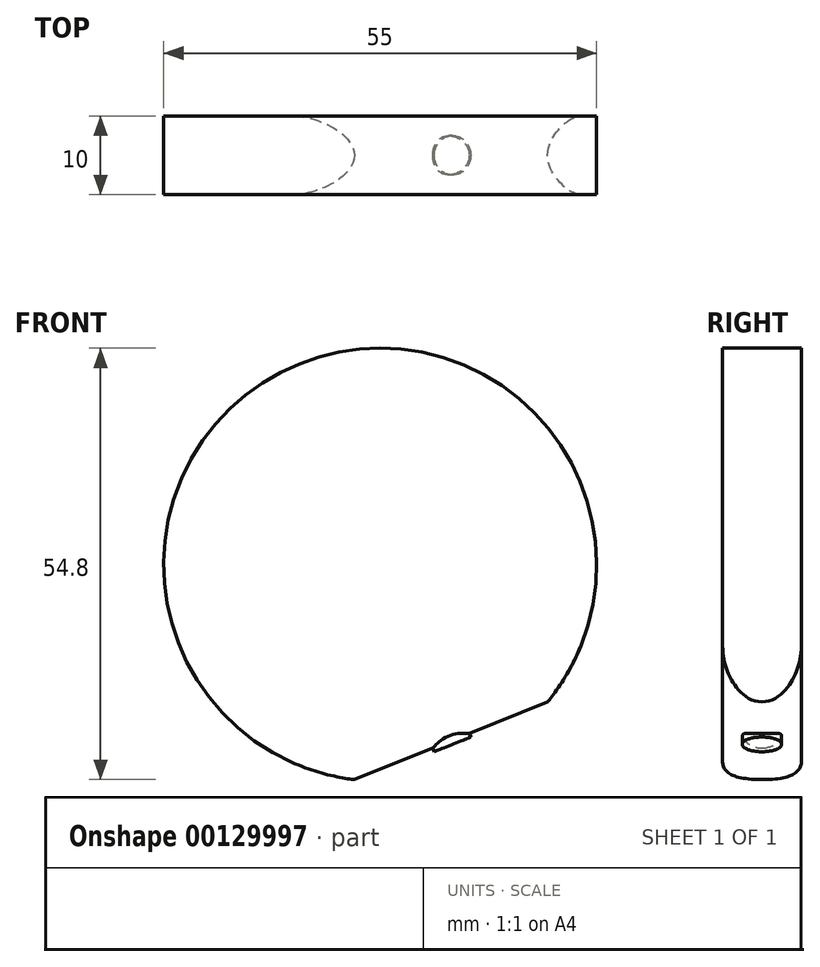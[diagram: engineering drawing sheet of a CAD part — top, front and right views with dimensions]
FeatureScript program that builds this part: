
annotation { "Feature Type Name" : "Feature", "Feature Type Description" : "" }
export const myFeature = defineFeature(function(context is Context, id is Id, definition is map)
    precondition{}
    {
        {
            var Q0;
            Q0=qCreatedBy(makeId("Front.planeOp"),FACE);
            var sketch = newSketch(context, id + "F0", { "sketchPlane" : qUnion([Q0])});
            skArc(sketch, "E0", {"start": v(5.8, 11.17) * mm, "mid": v(-25.73, 54.11) * mm, "end": v(-18.72, 1.3) * mm});
            skLineSegment(sketch, "E1", {"start": v(5.8, 11.17) * mm, "end": v(-18.72, 1.3) * mm});
            skSolve(sketch);
        }
        {
            var Q0;
            Q0=makeQuery(id+"F0.imprint","IMPRINT",FACE,{"disambiguationData":[TD([[makeQuery(id+"F0.imprint","IMPRINT",EDGE,{"derivedFrom":sQuery(id+"F0.wireOp",EDGE,"E0")}),1.0]])]});
            extrude(context, id + "F1", {"entities" : qUnion([Q0]), "depth" : 10 * mm});
        }
        {
            var Q0;
            Q0=makeQuery(id+"F1.opExtrude","SWEPT_FACE",FACE,{"disambiguationData":[OSD([sQuery(id+"F0.wireOp",EDGE,"E1")])]});
            var sketch = newSketch(context, id + "F2", { "sketchPlane" : qUnion([Q0])});
            skCircle(sketch, "E2", {"center": v(-3.67, 5) * mm, "radius": 2.5 * mm});
            skPoint(sketch, "E2.centerSnap0", {"position": v(-3.67, 10) * mm});
            skSolve(sketch);
        }
        {
            var Q0;
            Q0 = qSketchRegion(id + "F2", true);
            extrude(context, id + "F3", {"entities" : qUnion([Q0]), "operationType" : NewBodyOperationType.ADD, "depth" : 0.5 * mm});
        }
        {
            var Q0;
            Q0=makeQuery(id+"F1.opExtrude","CAP_EDGE",EDGE,{"disambiguationData":[OSD([sQuery(id+"F0.wireOp",EDGE,"E1")])],"isStart":false});
            var Q1;
            Q1=makeQuery(id+"F1.opExtrude","CAP_EDGE",EDGE,{"disambiguationData":[OSD([sQuery(id+"F0.wireOp",EDGE,"E1")])],"isStart":true});
            fillet(context, id + "F4", {"entities" : qUnion([Q0, Q1]), "radius" : 5 * mm, "tangentPropagation" : true, "allowEdgeOverflow" : false});
        }
    });
